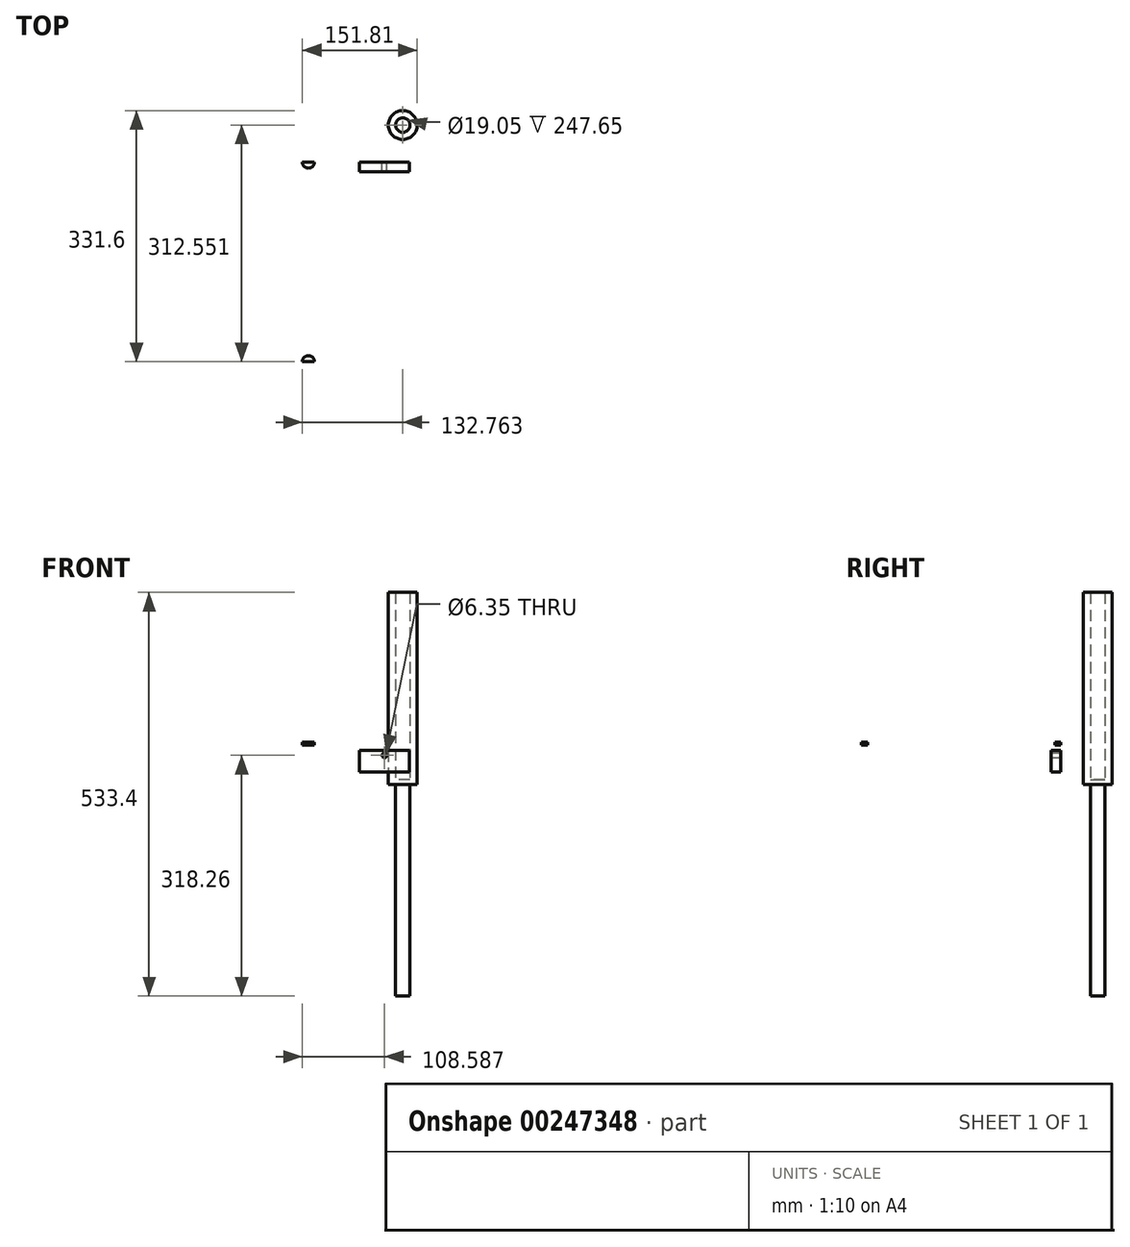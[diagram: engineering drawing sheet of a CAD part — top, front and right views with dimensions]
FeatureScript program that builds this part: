
annotation { "Feature Type Name" : "Feature", "Feature Type Description" : "" }
export const myFeature = defineFeature(function(context is Context, id is Id, definition is map)
    precondition{}
    {
        {
            var Q0;
            Q0=qCreatedBy(makeId("Front.planeOp"),FACE);
            var sketch = newSketch(context, id + "F0", { "sketchPlane" : qUnion([Q0])});
            skLineSegment(sketch, "E0.bottom", {"start": v(-126.6, 55.86) * mm, "end": v(-50.4, 55.86) * mm});
            skLineSegment(sketch, "E0.top", {"start": v(-126.6, 17.76) * mm, "end": v(-50.4, 17.76) * mm});
            skLineSegment(sketch, "E0.left", {"start": v(-126.6, 55.86) * mm, "end": v(-126.6, 17.76) * mm});
            skLineSegment(sketch, "E0.right", {"start": v(-50.4, 55.86) * mm, "end": v(-50.4, 17.76) * mm});
            skLineSegment(sketch, "E1", {"start": v(-121.52, 55.86) * mm, "end": v(-121.52, 17.76) * mm});
            skLineSegment(sketch, "E2", {"start": v(-126.6, 52.56) * mm, "end": v(-50.4, 52.56) * mm});
            skLineSegment(sketch, "E3", {"start": v(-88.5, 55.86) * mm, "end": v(-88.5, 17.76) * mm, "construction": true});
            skLineSegment(sketch, "E4.MirrorCS", {"start": v(-55.48, 55.86) * mm, "end": v(-55.48, 17.76) * mm});
            skSolve(sketch);
        }
        {
            var Q0;
            {var subQ0=sQuery(id+"F0.wireOp",EDGE,"E0.left");var subQ1=sQuery(id+"F0.wireOp",EDGE,"E0.bottom");var subQ2=makeQuery(id+"F0.imprint","INTERSECT",VERTEX,{"derivedFrom":[subQ1,subQ0]});Q0=makeQuery(id+"F0.imprint","IMPRINT",FACE,{"disambiguationData":[TD([[makeQuery(id+"F0.imprint","IMPRINT",EDGE,{"disambiguationData":[TD([[subQ2,-1.0]])],"derivedFrom":subQ1}),-1.0]])]});}
            var Q1;
            {var subQ0=sQuery(id+"F0.wireOp",EDGE,"E1");var subQ1=sQuery(id+"F0.wireOp",EDGE,"E0.bottom");var subQ2=makeQuery(id+"F0.imprint","INTERSECT",VERTEX,{"derivedFrom":[subQ1,subQ0]});Q1=makeQuery(id+"F0.imprint","IMPRINT",FACE,{"disambiguationData":[TD([[makeQuery(id+"F0.imprint","IMPRINT",EDGE,{"disambiguationData":[TD([[subQ2,-1.0]])],"derivedFrom":subQ1}),-1.0]])]});}
            var Q2;
            {var subQ0=sQuery(id+"F0.wireOp",EDGE,"E0.left");var subQ1=sQuery(id+"F0.wireOp",EDGE,"E0.top");var subQ2=makeQuery(id+"F0.imprint","INTERSECT",VERTEX,{"derivedFrom":[subQ1,subQ0]});Q2=makeQuery(id+"F0.imprint","IMPRINT",FACE,{"disambiguationData":[TD([[makeQuery(id+"F0.imprint","IMPRINT",EDGE,{"disambiguationData":[TD([[subQ2,-1.0]])],"derivedFrom":subQ1}),1.0]])]});}
            var Q3;
            {var subQ0=sQuery(id+"F0.wireOp",EDGE,"E0.right");var subQ1=sQuery(id+"F0.wireOp",EDGE,"E0.top");var subQ2=makeQuery(id+"F0.imprint","INTERSECT",VERTEX,{"derivedFrom":[subQ1,subQ0]});Q3=makeQuery(id+"F0.imprint","IMPRINT",FACE,{"disambiguationData":[TD([[makeQuery(id+"F0.imprint","IMPRINT",EDGE,{"disambiguationData":[TD([[subQ2,1.0]])],"derivedFrom":subQ1}),1.0]])]});}
            var Q4;
            {var subQ0=sQuery(id+"F0.wireOp",EDGE,"E0.right");var subQ1=sQuery(id+"F0.wireOp",EDGE,"E0.bottom");var subQ2=makeQuery(id+"F0.imprint","INTERSECT",VERTEX,{"derivedFrom":[subQ1,subQ0]});Q4=makeQuery(id+"F0.imprint","IMPRINT",FACE,{"disambiguationData":[TD([[makeQuery(id+"F0.imprint","IMPRINT",EDGE,{"disambiguationData":[TD([[subQ2,1.0]])],"derivedFrom":subQ1}),-1.0]])]});}
            extrude(context, id + "F1", {"entities" : qUnion([Q0, Q1, Q2, Q3, Q4]), "depth" : 263.52 * mm});
        }
        {
            var Q0;
            Q0=makeQuery(id+"F1.opExtrude","SWEPT_FACE",FACE,{"disambiguationData":[OSD([sQuery(id+"F0.wireOp",EDGE,"E0.bottom")])]});
            var sketch = newSketch(context, id + "F2", { "sketchPlane" : qUnion([Q0])});
            skCircle(sketch, "E5", {"center": v(-88.5, -131.76) * mm, "radius": 19.05 * mm});
            skPoint(sketch, "E5.centerSnap0", {"position": v(-88.5, 0) * mm});
            skPoint(sketch, "E5.centerSnap1", {"position": v(-50.4, -131.76) * mm});
            skCircle(sketch, "E6", {"center": v(-88.5, 0) * mm, "radius": 7.94 * mm});
            skLineSegment(sketch, "E7", {"start": v(-50.4, -131.76) * mm, "end": v(-126.6, -131.76) * mm, "construction": true});
            skCircle(sketch, "E8.MirrorC", {"center": v(-88.5, -263.53) * mm, "radius": 7.94 * mm});
            skSolve(sketch);
        }
        {
            var Q0;
            Q0=makeQuery(id+"F2.imprint","IMPRINT",FACE,{"disambiguationData":[TD([[makeQuery(id+"F2.imprint","IMPRINT",EDGE,{"derivedFrom":sQuery(id+"F2.wireOp",EDGE,"E5")}),1.0]])]});
            var Q1;
            {var subQ0=sQuery(id+"F2.wireOp",EDGE,"E6");var subQ1=makeQuery(id+"F1.opExtrude","CAP_EDGE",EDGE,{"disambiguationData":[OSD([sQuery(id+"F0.wireOp",EDGE,"E0.bottom")])],"isStart":true});var subQ2=makeQuery(id+"F2.imprint","INTERSECT",VERTEX,{"disambiguationData":[OD(0.0)],"derivedFrom":[subQ1,subQ0]});Q1=makeQuery(id+"F2.imprint","IMPRINT",FACE,{"disambiguationData":[TD([[makeQuery(id+"F2.imprint","IMPRINT",EDGE,{"disambiguationData":[TD([[subQ2,-1.0]])],"derivedFrom":subQ0}),1.0]])]});}
            var Q2;
            {var subQ0=sQuery(id+"F2.wireOp",EDGE,"E8.MirrorC");var subQ1=makeQuery(id+"F1.opExtrude","CAP_EDGE",EDGE,{"disambiguationData":[OSD([sQuery(id+"F0.wireOp",EDGE,"E0.bottom")])],"isStart":false});var subQ2=makeQuery(id+"F2.imprint","INTERSECT",VERTEX,{"disambiguationData":[OD(0.0)],"derivedFrom":[subQ1,subQ0]});Q2=makeQuery(id+"F2.imprint","IMPRINT",FACE,{"disambiguationData":[TD([[makeQuery(id+"F2.imprint","IMPRINT",EDGE,{"disambiguationData":[TD([[subQ2,-1.0]])],"derivedFrom":subQ0}),-1.0]])]});}
            extrude(context, id + "F3", {"entities" : qUnion([Q0, Q1, Q2]), "operationType" : NewBodyOperationType.REMOVE, "endBound" : BoundingType.THROUGH_ALL, "oppositeDirection" : true, "depth" : 25.4 * mm});
        }
        {
            var Q0;
            Q0=qCreatedBy(makeId("Front.planeOp"),FACE);
            var sketch = newSketch(context, id + "F4", { "sketchPlane" : qUnion([Q0])});
            skLineSegment(sketch, "E9.bottom", {"start": v(-20.87, 45.2) * mm, "end": v(45.17, 45.2) * mm});
            skLineSegment(sketch, "E9.top", {"start": v(-20.87, 16.63) * mm, "end": v(45.17, 16.63) * mm});
            skLineSegment(sketch, "E9.left", {"start": v(-20.87, 45.2) * mm, "end": v(-20.87, 16.63) * mm});
            skLineSegment(sketch, "E9.right", {"start": v(45.17, 45.2) * mm, "end": v(45.17, 16.63) * mm});
            skLineSegment(sketch, "E10", {"start": v(12.15, 45.2) * mm, "end": v(12.15, 16.63) * mm, "construction": true});
            skCircle(sketch, "E11", {"center": v(12.15, 38.86) * mm, "radius": 3.18 * mm});
            skSolve(sketch);
        }
        {
            var Q0;
            Q0=makeQuery(id+"F4.imprint","IMPRINT",FACE,{"disambiguationData":[TD([[makeQuery(id+"F4.imprint","IMPRINT",EDGE,{"derivedFrom":sQuery(id+"F4.wireOp",EDGE,"E9.bottom")}),-1.0]])]});
            extrude(context, id + "F5", {"entities" : qUnion([Q0]), "depth" : 12.7 * mm});
        }
        {
            var Q0;
            Q0=qCreatedBy(makeId("Top.planeOp"),FACE);
            var sketch = newSketch(context, id + "F6", { "sketchPlane" : qUnion([Q0])});
            skCircle(sketch, "E12", {"center": v(36.32, 49.02) * mm, "radius": 19.05 * mm});
            skCircle(sketch, "E13", {"center": v(36.32, 49.02) * mm, "radius": 9.53 * mm});
            skSolve(sketch);
        }
        {
            var Q0;
            Q0=makeQuery(id+"F6.imprint","IMPRINT",FACE,{"disambiguationData":[TD([[makeQuery(id+"F6.imprint","IMPRINT",EDGE,{"derivedFrom":sQuery(id+"F6.wireOp",EDGE,"E12")}),-1.0]])]});
            var Q1;
            Q1=makeQuery(id+"F6.imprint","IMPRINT",FACE,{"disambiguationData":[TD([[makeQuery(id+"F6.imprint","IMPRINT",EDGE,{"derivedFrom":sQuery(id+"F6.wireOp",EDGE,"E12")}),1.0]])]});
            extrude(context, id + "F7", {"entities" : qUnion([Q0, Q1]), "depth" : 254 * mm});
        }
        {
            var Q0;
            Q0=makeQuery(id+"F6.imprint","IMPRINT",FACE,{"disambiguationData":[TD([[makeQuery(id+"F6.imprint","IMPRINT",EDGE,{"derivedFrom":sQuery(id+"F6.wireOp",EDGE,"E13")}),1.0]])]});
            extrude(context, id + "F8", {"entities" : qUnion([Q0]), "operationType" : NewBodyOperationType.ADD, "depth" : 6.35 * mm});
        }
        {
            var Q0;
            Q0=makeQuery(id+"F6.imprint","IMPRINT",FACE,{"disambiguationData":[TD([[makeQuery(id+"F6.imprint","IMPRINT",EDGE,{"derivedFrom":sQuery(id+"F6.wireOp",EDGE,"E13")}),1.0]])]});
            extrude(context, id + "F9", {"entities" : qUnion([Q0]), "oppositeDirection" : true, "depth" : 279.4 * mm});
        }
    });
